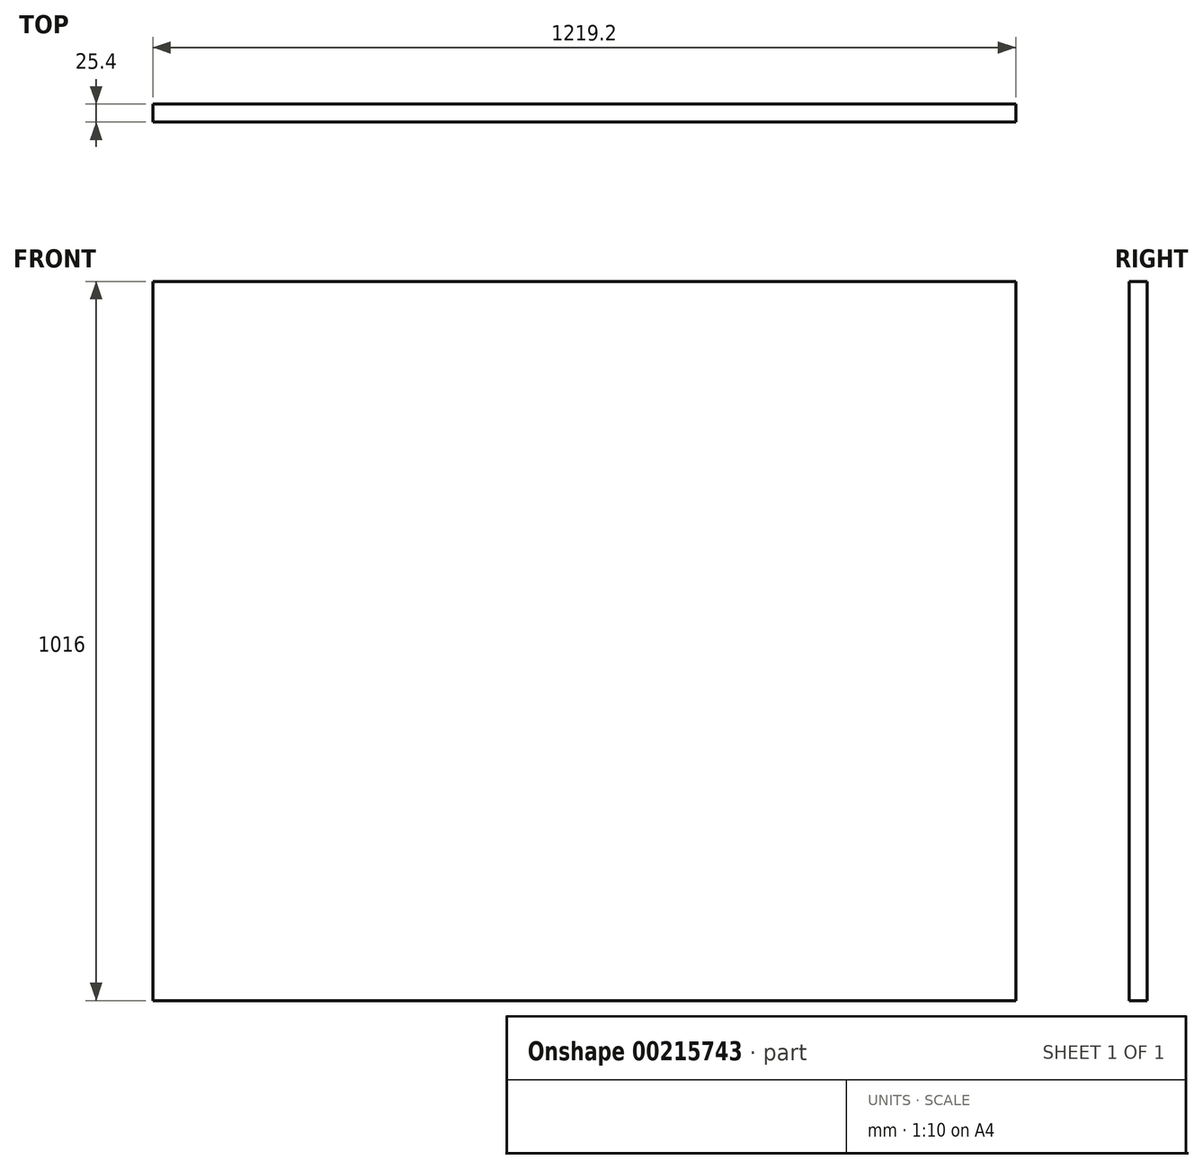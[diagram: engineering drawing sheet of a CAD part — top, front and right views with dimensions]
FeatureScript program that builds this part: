
annotation { "Feature Type Name" : "Feature", "Feature Type Description" : "" }
export const myFeature = defineFeature(function(context is Context, id is Id, definition is map)
    precondition{}
    {
        {
            var Q0;
            Q0=qCreatedBy(makeId("Front.planeOp"),FACE);
            var sketch = newSketch(context, id + "F0", { "sketchPlane" : qUnion([Q0])});
            skLineSegment(sketch, "E0.bottom", {"start": v(0, 0) * mm, "end": v(1219.2, 0) * mm});
            skLineSegment(sketch, "E0.top", {"start": v(0, -1016) * mm, "end": v(1219.2, -1016) * mm});
            skLineSegment(sketch, "E0.left", {"start": v(0, 0) * mm, "end": v(0, -1016) * mm});
            skLineSegment(sketch, "E0.right", {"start": v(1219.2, 0) * mm, "end": v(1219.2, -1016) * mm});
            skSolve(sketch);
        }
        {
            var Q0;
            Q0 = qSketchRegion(id + "F0", true);
            extrude(context, id + "F1", {"entities" : qUnion([Q0]), "oppositeDirection" : true, "depth" : 25.4 * mm});
        }
    });
